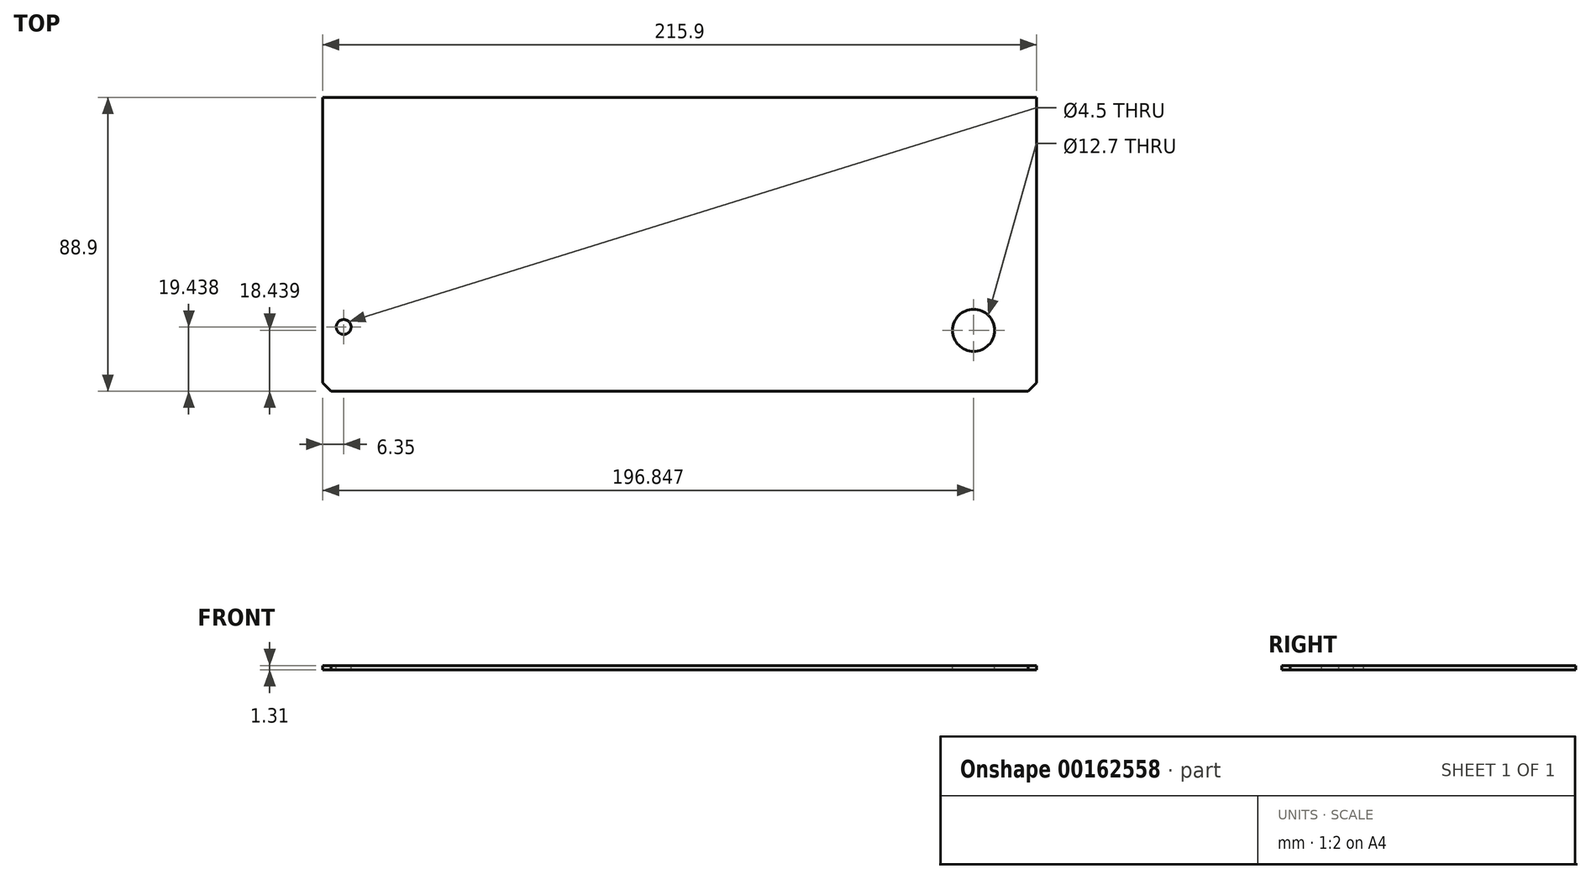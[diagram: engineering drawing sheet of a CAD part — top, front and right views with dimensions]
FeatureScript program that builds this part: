
annotation { "Feature Type Name" : "Feature", "Feature Type Description" : "" }
export const myFeature = defineFeature(function(context is Context, id is Id, definition is map)
    precondition{}
    {
        {
            var Q0;
            Q0=qCreatedBy(makeId("Top.planeOp"),FACE);
            var sketch = newSketch(context, id + "F0", { "sketchPlane" : qUnion([Q0])});
            skLineSegment(sketch, "E0.bottom", {"start": v(-105.24, -56.6) * mm, "end": v(110.66, -56.6) * mm});
            skLineSegment(sketch, "E0.top", {"start": v(-105.24, 32.3) * mm, "end": v(110.66, 32.3) * mm});
            skLineSegment(sketch, "E0.left", {"start": v(-105.24, -56.6) * mm, "end": v(-105.24, 32.3) * mm});
            skLineSegment(sketch, "E0.right", {"start": v(110.66, -56.6) * mm, "end": v(110.66, 32.3) * mm});
            skSolve(sketch);
        }
        {
            var Q0;
            Q0=makeQuery(id+"F0.imprint","IMPRINT",FACE,{"disambiguationData":[TD([[makeQuery(id+"F0.imprint","IMPRINT",EDGE,{"derivedFrom":sQuery(id+"F0.wireOp",EDGE,"E0.bottom")}),1.0]])]});
            extrude(context, id + "F1", {"entities" : qUnion([Q0]), "oppositeDirection" : true, "depth" : 1.31 * mm});
        }
        {
            var Q0;
            Q0=makeQuery(id+"F1.opExtrude","SWEPT_EDGE",EDGE,{"disambiguationData":[OSD([sQuery(id+"F0.wireOp",EDGE,"E0.bottom"),sQuery(id+"F0.wireOp",EDGE,"E0.left")])]});
            chamfer(context, id + "F2", {"entities" : qUnion([Q0]), "width" : 2.54 * mm, "tangentPropagation" : true});
        }
        {
            var Q0;
            Q0=makeQuery(id+"F1.opExtrude","SWEPT_EDGE",EDGE,{"disambiguationData":[OSD([sQuery(id+"F0.wireOp",EDGE,"E0.bottom"),sQuery(id+"F0.wireOp",EDGE,"E0.right")])]});
            chamfer(context, id + "F3", {"entities" : qUnion([Q0]), "width" : 2.54 * mm, "tangentPropagation" : true});
        }
        {
            var Q0;
            Q0=makeQuery(id+"F0.imprint","IMPRINT",FACE,{"disambiguationData":[TD([[makeQuery(id+"F0.imprint","IMPRINT",EDGE,{"derivedFrom":sQuery(id+"F0.wireOp",EDGE,"E0.bottom")}),1.0]])]});
            var sketch = newSketch(context, id + "F4", { "sketchPlane" : qUnion([Q0])});
            skLineSegment(sketch, "E1", {"start": v(-98.9, -37.15) * mm, "end": v(91.6, -38.15) * mm});
            skSolve(sketch);
        }
        {
            var Q0;
            Q0=sQuery(id+"F4.wireOp",VERTEX,"E1.start");
            var Q1;
            Q1=makeQuery(id+"F1.opExtrude","SWEPT_BODY",BODY,{"disambiguationData":[OSD([sQuery(id+"F0.wireOp",EDGE,"E0.bottom"),sQuery(id+"F0.wireOp",EDGE,"E0.top"),sQuery(id+"F0.wireOp",EDGE,"E0.left"),sQuery(id+"F0.wireOp",EDGE,"E0.right")])]});
            hole(context, id + "F5", {"style" : HoleStyle.SIMPLE, "endStyle" : HoleEndStyle.THROUGH, "holeDiameter" : 4.5 * mm, "locations" : qUnion([Q0]), "scope" : qUnion([Q1]), "isTappedThrough" : true});
        }
        {
            var Q0;
            Q0=sQuery(id+"F4.wireOp",VERTEX,"E1.end");
            var Q1;
            Q1=makeQuery(id+"F1.opExtrude","SWEPT_BODY",BODY,{"disambiguationData":[OSD([sQuery(id+"F0.wireOp",EDGE,"E0.bottom"),sQuery(id+"F0.wireOp",EDGE,"E0.top"),sQuery(id+"F0.wireOp",EDGE,"E0.left"),sQuery(id+"F0.wireOp",EDGE,"E0.right")])]});
            hole(context, id + "F6", {"style" : HoleStyle.SIMPLE, "endStyle" : HoleEndStyle.THROUGH, "holeDiameter" : 12.7 * mm, "locations" : qUnion([Q0]), "scope" : qUnion([Q1]), "isTappedThrough" : true});
        }
    });
